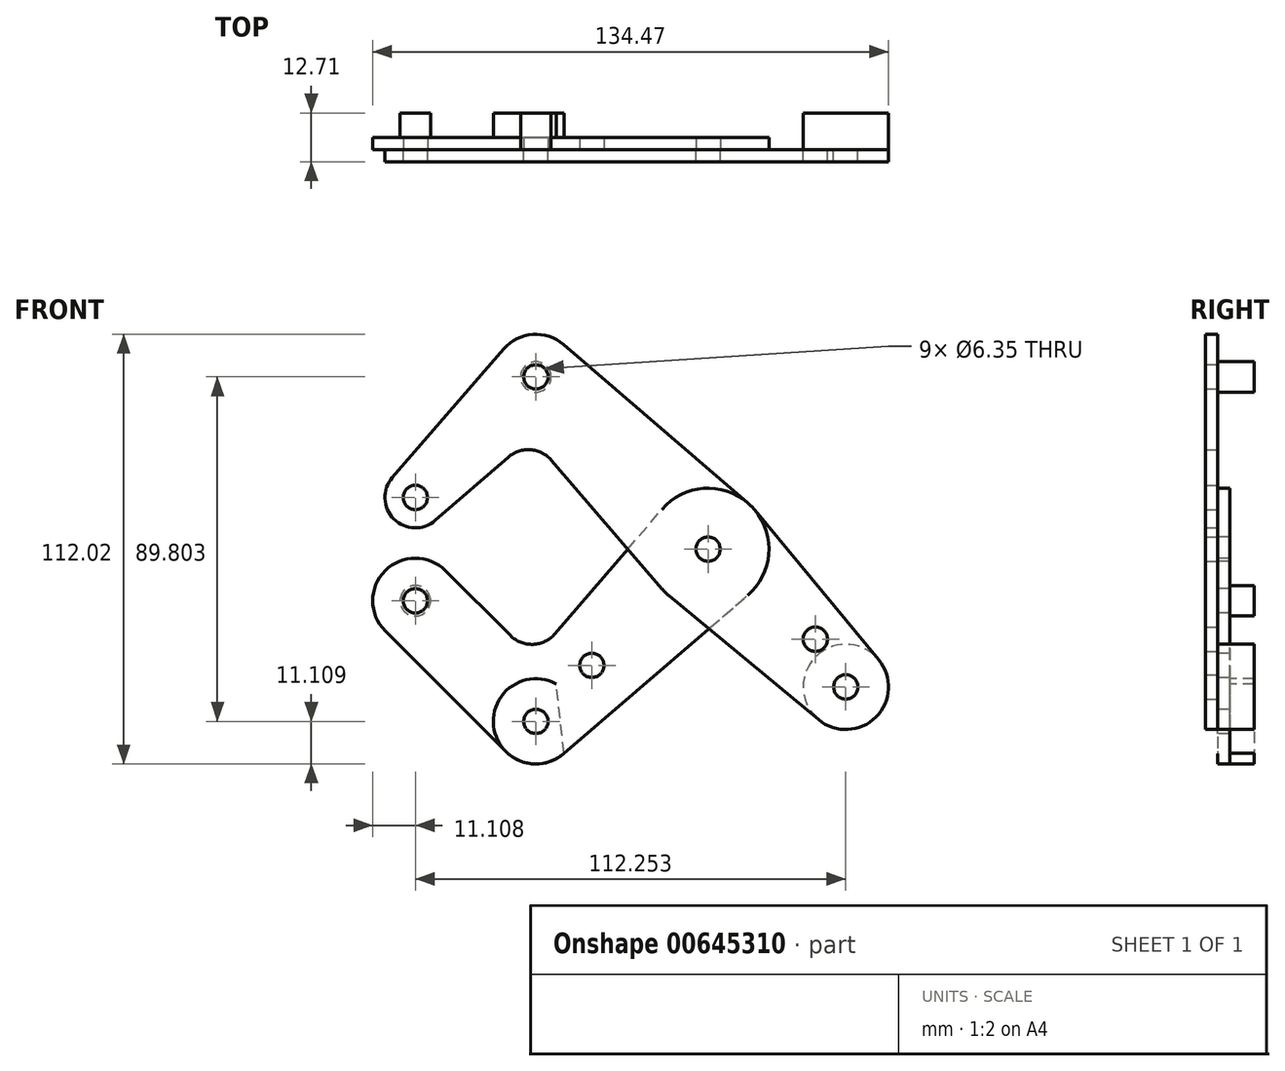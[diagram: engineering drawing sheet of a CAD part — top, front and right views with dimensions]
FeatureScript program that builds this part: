
annotation { "Feature Type Name" : "Feature", "Feature Type Description" : "" }
export const myFeature = defineFeature(function(context is Context, id is Id, definition is map)
    precondition{}
    {
        {
            var Q0;
            Q0=qCreatedBy(makeId("Front.planeOp"),FACE);
            var sketch = newSketch(context, id + "F0", { "sketchPlane" : qUnion([Q0])});
            skLineSegment(sketch, "E0", {"start": v(-76.33, 13.47) * mm, "end": v(-44.9, 44.9) * mm, "construction": true});
            skLineSegment(sketch, "E1", {"start": v(-44.9, 44.9) * mm, "end": v(35.92, -35.92) * mm, "construction": true});
            skCircle(sketch, "E2", {"center": v(-76.33, 13.47) * mm, "radius": 7.94 * mm});
            skCircle(sketch, "E3", {"center": v(-44.9, 44.9) * mm, "radius": 11.11 * mm});
            skCircle(sketch, "E4", {"center": v(-44.9, 44.9) * mm, "radius": 3.18 * mm});
            skCircle(sketch, "E5", {"center": v(0, 0) * mm, "radius": 15.88 * mm});
            skCircle(sketch, "E6", {"center": v(0, 0) * mm, "radius": 3.98 * mm});
            skCircle(sketch, "E7", {"center": v(35.92, -35.92) * mm, "radius": 11.11 * mm});
            skCircle(sketch, "E8", {"center": v(35.92, -35.92) * mm, "radius": 3.18 * mm});
            skCircle(sketch, "E9", {"center": v(-76.33, 13.47) * mm, "radius": 3.18 * mm});
            skCircle(sketch, "E10", {"center": v(27.97, -23.48) * mm, "radius": 3.17 * mm});
            skLineSegment(sketch, "E11", {"start": v(-82.33, 18.67) * mm, "end": v(-53.3, 52.18) * mm});
            skLineSegment(sketch, "E12", {"start": v(-71.13, 7.47) * mm, "end": v(-52.08, 23.98) * mm});
            skLineSegment(sketch, "E13", {"start": v(-37.66, 53.33) * mm, "end": v(10.35, 12.04) * mm});
            skLineSegment(sketch, "E14", {"start": v(-40.85, 23.15) * mm, "end": v(-12.04, -10.35) * mm});
            skCircle(sketch, "E15", {"center": v(0, 0) * mm, "radius": 3.18 * mm});
            skLineSegment(sketch, "E16", {"start": v(-10.12, -12.23) * mm, "end": v(28.83, -44.48) * mm});
            skLineSegment(sketch, "E17", {"start": v(12.23, 10.12) * mm, "end": v(44.48, -28.83) * mm});
            skPoint(sketch, "E18.newPointA", {"position": v(-37.08, 36.98) * mm});
            skPoint(sketch, "E18.newPointB", {"position": v(-52.74, 36.98) * mm});
            skArc(sketch, "E18.filletArc", {"start": v(-40.85, 23.15) * mm, "mid": v(-46.3, 25.9) * mm, "end": v(-52.08, 23.98) * mm});
            skLineSegment(sketch, "E19", {"start": v(0, 0) * mm, "end": v(-44.9, -44.9) * mm, "construction": true});
            skLineSegment(sketch, "E20", {"start": v(-44.9, -44.9) * mm, "end": v(-76.33, -13.47) * mm, "construction": true});
            skCircle(sketch, "E21", {"center": v(-76.33, -13.47) * mm, "radius": 11.11 * mm});
            skCircle(sketch, "E22", {"center": v(-76.33, -13.47) * mm, "radius": 3.18 * mm});
            skCircle(sketch, "E23", {"center": v(-44.9, -44.9) * mm, "radius": 11.11 * mm});
            skCircle(sketch, "E24", {"center": v(-44.9, -44.9) * mm, "radius": 3.18 * mm});
            skCircle(sketch, "E25", {"center": v(-30.3, -30.3) * mm, "radius": 3.18 * mm});
            skLineSegment(sketch, "E26", {"start": v(-84.19, -21.33) * mm, "end": v(-52.76, -52.76) * mm});
            skLineSegment(sketch, "E27", {"start": v(-68.47, -5.61) * mm, "end": v(-51.57, -22.51) * mm});
            skLineSegment(sketch, "E28", {"start": v(-39.93, -22.07) * mm, "end": v(-12.04, 10.35) * mm});
            skLineSegment(sketch, "E29", {"start": v(-37.66, -53.33) * mm, "end": v(10.35, -12.04) * mm});
            skArc(sketch, "E30.filletArc", {"start": v(-51.57, -22.51) * mm, "mid": v(-45.65, -24.84) * mm, "end": v(-39.93, -22.07) * mm});
            skSolve(sketch);
        }
        {
            var Q0;
            {var subQ0=sQuery(id+"F0.wireOp",EDGE,"E11");Q0=makeQuery(id+"F0.imprint","IMPRINT",FACE,{"disambiguationData":[TD([[makeQuery(id+"F0.imprint","IMPRINT",EDGE,{"derivedFrom":subQ0}),-1.0]])]});}
            var Q1;
            Q1=makeQuery(id+"F0.imprint","IMPRINT",FACE,{"disambiguationData":[TD([[makeQuery(id+"F0.imprint","IMPRINT",EDGE,{"derivedFrom":sQuery(id+"F0.wireOp",EDGE,"E4")}),-1.0]])]});
            var Q2;
            Q2=makeQuery(id+"F0.imprint","IMPRINT",FACE,{"disambiguationData":[TD([[makeQuery(id+"F0.imprint","IMPRINT",EDGE,{"derivedFrom":sQuery(id+"F0.wireOp",EDGE,"E6")}),-1.0]])]});
            var Q3;
            {var subQ0=sQuery(id+"F0.wireOp",EDGE,"E14");var subQ1=sQuery(id+"F0.wireOp",EDGE,"E5");var subQ2=makeQuery(id+"F0.imprint","INTERSECT",VERTEX,{"derivedFrom":[subQ1,subQ0]});Q3=makeQuery(id+"F0.imprint","IMPRINT",FACE,{"disambiguationData":[TD([[makeQuery(id+"F0.imprint","IMPRINT",EDGE,{"disambiguationData":[TD([[subQ2,1.0]])],"derivedFrom":subQ1}),-1.0]])]});}
            var Q4;
            {var subQ0=sQuery(id+"F0.wireOp",EDGE,"E16");var subQ1=sQuery(id+"F0.wireOp",EDGE,"E5");var subQ2=makeQuery(id+"F0.imprint","INTERSECT",VERTEX,{"derivedFrom":[subQ1,subQ0]});Q4=makeQuery(id+"F0.imprint","IMPRINT",FACE,{"disambiguationData":[TD([[makeQuery(id+"F0.imprint","IMPRINT",EDGE,{"disambiguationData":[TD([[subQ2,-1.0]])],"derivedFrom":subQ1}),-1.0]])]});}
            var Q5;
            Q5=makeQuery(id+"F0.imprint","IMPRINT",FACE,{"disambiguationData":[TD([[makeQuery(id+"F0.imprint","IMPRINT",EDGE,{"derivedFrom":sQuery(id+"F0.wireOp",EDGE,"E10")}),-1.0]])]});
            var Q6;
            Q6=makeQuery(id+"F0.imprint","IMPRINT",FACE,{"disambiguationData":[TD([[makeQuery(id+"F0.imprint","IMPRINT",EDGE,{"derivedFrom":sQuery(id+"F0.wireOp",EDGE,"E8")}),-1.0]])]});
            var Q7;
            Q7=makeQuery(id+"F0.imprint","IMPRINT",FACE,{"disambiguationData":[TD([[makeQuery(id+"F0.imprint","IMPRINT",EDGE,{"derivedFrom":sQuery(id+"F0.wireOp",EDGE,"E9")}),-1.0]])]});
            var Q8;
            Q8=makeQuery(id+"F0.imprint","IMPRINT",FACE,{"disambiguationData":[TD([[makeQuery(id+"F0.imprint","IMPRINT",EDGE,{"derivedFrom":sQuery(id+"F0.wireOp",EDGE,"E6")}),1.0]])]});
            extrude(context, id + "F1", {"entities" : qUnion([Q0, Q1, Q2, Q3, Q4, Q5, Q6, Q7, Q8]), "depth" : 3.17 * mm, "offsetDistance" : 25.4 * mm});
        }
        {
            var Q0;
            Q0=makeQuery(id+"F0.imprint","IMPRINT",FACE,{"disambiguationData":[TD([[makeQuery(id+"F0.imprint","IMPRINT",EDGE,{"derivedFrom":sQuery(id+"F0.wireOp",EDGE,"E22")}),-1.0]])]});
            var Q1;
            Q1=makeQuery(id+"F0.imprint","IMPRINT",FACE,{"disambiguationData":[TD([[makeQuery(id+"F0.imprint","IMPRINT",EDGE,{"derivedFrom":sQuery(id+"F0.wireOp",EDGE,"E25")}),-1.0]])]});
            var Q2;
            {var subQ0=sQuery(id+"F0.wireOp",EDGE,"E16");var subQ1=sQuery(id+"F0.wireOp",EDGE,"E5");var subQ2=makeQuery(id+"F0.imprint","INTERSECT",VERTEX,{"derivedFrom":[subQ1,subQ0]});Q2=makeQuery(id+"F0.imprint","IMPRINT",FACE,{"disambiguationData":[TD([[makeQuery(id+"F0.imprint","IMPRINT",EDGE,{"disambiguationData":[TD([[subQ2,-1.0]])],"derivedFrom":subQ1}),-1.0]])]});}
            var Q3;
            {var subQ0=sQuery(id+"F0.wireOp",EDGE,"E14");var subQ1=sQuery(id+"F0.wireOp",EDGE,"E5");var subQ2=makeQuery(id+"F0.imprint","INTERSECT",VERTEX,{"derivedFrom":[subQ1,subQ0]});Q3=makeQuery(id+"F0.imprint","IMPRINT",FACE,{"disambiguationData":[TD([[makeQuery(id+"F0.imprint","IMPRINT",EDGE,{"disambiguationData":[TD([[subQ2,1.0]])],"derivedFrom":subQ1}),-1.0]])]});}
            var Q4;
            Q4=makeQuery(id+"F0.imprint","IMPRINT",FACE,{"disambiguationData":[TD([[makeQuery(id+"F0.imprint","IMPRINT",EDGE,{"derivedFrom":sQuery(id+"F0.wireOp",EDGE,"E6")}),-1.0]])]});
            var Q5;
            Q5=makeQuery(id+"F0.imprint","IMPRINT",FACE,{"disambiguationData":[TD([[makeQuery(id+"F0.imprint","IMPRINT",EDGE,{"derivedFrom":sQuery(id+"F0.wireOp",EDGE,"E24")}),-1.0]])]});
            var Q6;
            Q6=makeQuery(id+"F0.imprint","IMPRINT",FACE,{"disambiguationData":[TD([[makeQuery(id+"F0.imprint","IMPRINT",EDGE,{"derivedFrom":sQuery(id+"F0.wireOp",EDGE,"E6")}),1.0]])]});
            extrude(context, id + "F2", {"entities" : qUnion([Q0, Q1, Q2, Q3, Q4, Q5, Q6]), "oppositeDirection" : true, "depth" : 3.17 * mm, "offsetDistance" : 25.4 * mm});
        }
        {
            var Q0;
            Q0=makeQuery(id+"F1.opExtrude","CAP_FACE",FACE,{"disambiguationData":[OSD([sQuery(id+"F0.wireOp",EDGE,"E2"),sQuery(id+"F0.wireOp",EDGE,"E3"),sQuery(id+"F0.wireOp",EDGE,"E4"),sQuery(id+"F0.wireOp",EDGE,"E5"),sQuery(id+"F0.wireOp",EDGE,"E7"),sQuery(id+"F0.wireOp",EDGE,"E8"),sQuery(id+"F0.wireOp",EDGE,"E9"),sQuery(id+"F0.wireOp",EDGE,"E10"),sQuery(id+"F0.wireOp",EDGE,"E11"),sQuery(id+"F0.wireOp",EDGE,"E12"),sQuery(id+"F0.wireOp",EDGE,"E13"),sQuery(id+"F0.wireOp",EDGE,"E14"),sQuery(id+"F0.wireOp",EDGE,"E15"),sQuery(id+"F0.wireOp",EDGE,"E16"),sQuery(id+"F0.wireOp",EDGE,"E17"),sQuery(id+"F0.wireOp",EDGE,"E18.filletArc")])],"isStart":false});
            var sketch = newSketch(context, id + "F3", { "sketchPlane" : qUnion([Q0])});
            skCircle(sketch, "E31", {"center": v(-44.9, 44.9) * mm, "radius": 3.98 * mm});
            skCircle(sketch, "E32.0", {"center": v(35.92, -35.92) * mm, "radius": 11.11 * mm});
            skSolve(sketch);
        }
        {
            var Q0;
            Q0=makeQuery(id+"F0.imprint","IMPRINT",FACE,{"disambiguationData":[TD([[makeQuery(id+"F0.imprint","IMPRINT",EDGE,{"derivedFrom":sQuery(id+"F0.wireOp",EDGE,"E22")}),-1.0]])]});
            var sketch = newSketch(context, id + "F4", { "sketchPlane" : qUnion([Q0])});
            skCircle(sketch, "E33", {"center": v(-76.33, -13.47) * mm, "radius": 3.98 * mm});
            skArc(sketch, "E34.0", {"start": v(-39.6, -35.14) * mm, "mid": v(-55.95, -46.13) * mm, "end": v(-37.58, -53.26) * mm});
            skLineSegment(sketch, "E35", {"start": v(-44.9, -44.9) * mm, "end": v(35.92, -35.92) * mm, "construction": true});
            skLineSegment(sketch, "E36", {"start": v(-39.6, -35.14) * mm, "end": v(-37.58, -53.26) * mm});
            skSolve(sketch);
        }
        {
            var Q0;
            Q0=qCreatedBy(makeId("Front.planeOp"),FACE);
            cPlane(context, id + "F5", {"entities" : qUnion([Q0]), "cplaneType" : CPlaneType.OFFSET, "offset" : 9.52 * mm, "oppositeDirection" : true, "width" : 152.4 * mm, "height" : 152.4 * mm});
        }
        {
            var Q0;
            Q0 = qSketchRegion(id + "F3", true);
            var Q1;
            Q1 = qSketchRegion(id + "F4", true);
            var Q2;
            Q2=qCreatedBy(id+"F5.planeOp",FACE);
            extrude(context, id + "F6", {"entities" : qUnion([Q0, Q1]), "endBound" : BoundingType.UP_TO_SURFACE, "oppositeDirection" : true, "depth" : 25.4 * mm, "endBoundEntityFace" : qUnion([Q2]), "offsetDistance" : 25.4 * mm});
        }
        {
            var Q0;
            Q0=makeQuery(id+"F1.opExtrude","SWEPT_BODY",BODY,{"disambiguationData":[OSD([sQuery(id+"F0.wireOp",EDGE,"E2"),sQuery(id+"F0.wireOp",EDGE,"E3"),sQuery(id+"F0.wireOp",EDGE,"E4"),sQuery(id+"F0.wireOp",EDGE,"E5"),sQuery(id+"F0.wireOp",EDGE,"E7"),sQuery(id+"F0.wireOp",EDGE,"E8"),sQuery(id+"F0.wireOp",EDGE,"E9"),sQuery(id+"F0.wireOp",EDGE,"E10"),sQuery(id+"F0.wireOp",EDGE,"E11"),sQuery(id+"F0.wireOp",EDGE,"E12"),sQuery(id+"F0.wireOp",EDGE,"E13"),sQuery(id+"F0.wireOp",EDGE,"E14"),sQuery(id+"F0.wireOp",EDGE,"E15"),sQuery(id+"F0.wireOp",EDGE,"E16"),sQuery(id+"F0.wireOp",EDGE,"E17"),sQuery(id+"F0.wireOp",EDGE,"E18.filletArc")])]});
            var Q1;
            Q1=makeQuery(id+"F2.opExtrude","SWEPT_BODY",BODY,{"disambiguationData":[OSD([sQuery(id+"F0.wireOp",EDGE,"E5"),sQuery(id+"F0.wireOp",EDGE,"E15"),sQuery(id+"F0.wireOp",EDGE,"E21"),sQuery(id+"F0.wireOp",EDGE,"E22"),sQuery(id+"F0.wireOp",EDGE,"E23"),sQuery(id+"F0.wireOp",EDGE,"E24"),sQuery(id+"F0.wireOp",EDGE,"E25"),sQuery(id+"F0.wireOp",EDGE,"E26"),sQuery(id+"F0.wireOp",EDGE,"E27"),sQuery(id+"F0.wireOp",EDGE,"E28"),sQuery(id+"F0.wireOp",EDGE,"E29"),sQuery(id+"F0.wireOp",EDGE,"E30.filletArc")])]});
            var Q2;
            Q2=makeQuery(id+"F6.opExtrude","SWEPT_BODY",BODY,{"disambiguationData":[OSD([sQuery(id+"F4.wireOp",EDGE,"E33")])]});
            var Q3;
            Q3=makeQuery(id+"F6.opExtrude","SWEPT_BODY",BODY,{"disambiguationData":[OSD([sQuery(id+"F3.wireOp",EDGE,"E31")])]});
            var Q4;
            Q4=makeQuery(id+"F6.opExtrude","SWEPT_BODY",BODY,{"disambiguationData":[OSD([sQuery(id+"F3.wireOp",EDGE,"E32.0")])]});
            var Q5;
            Q5=makeQuery(id+"F6.opExtrude","SWEPT_BODY",BODY,{"disambiguationData":[OSD([sQuery(id+"F4.wireOp",EDGE,"E34.0"),sQuery(id+"F4.wireOp",EDGE,"E36")])]});
            booleanBodies(context, id + "F7", {"operationType" : BooleanOperationType.SUBTRACTION, "tools" : qUnion([Q0, Q1]), "targets" : qUnion([Q2, Q3, Q4, Q5]), "keepTools" : true});
        }
    });
